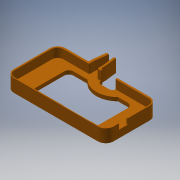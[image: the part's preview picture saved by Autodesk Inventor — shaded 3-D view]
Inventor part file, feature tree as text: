
AUTODESK INVENTOR PART (.ipt)
format: ipt  version: 2017 (Build 210142000, 142)  size: 312,832 bytes
history: native  units: in
note: dims shown in document units (in); Inventor stores cm internally (conversion verified against a paired STEP export)
features: extrude x11, sketch x11, fillet x7, thicken_offset x1
ambient origin geometry x8: Origin, YZ Plane, XZ Plane, XY Plane, X Axis, Y Axis, Z Axis, Center Point
bodies: Solid1 (feature_tree)
feature tree (30):
  extrude  "Extrusion1"  Depth=2.655in
  extrude  "Extrusion2"  Depth=0.5in TaperAngle=0.0deg
  fillet  "Fillet1"  Radius=0.2in
  fillet  "Fillet2"  Radius=0.3in
  extrude  "Extrusion3"  Depth=0.42in
  extrude  "Extrusion4"  Depth=0.125in
  extrude  "Extrusion5"  Depth=0.125in
  fillet  "Fillet3"  Radius=0.125in
  fillet  "Fillet4"  Radius=0.125in
  fillet  "Fillet5"  Radius=0.125in
  extrude  "Extrusion6"  Depth=0.125in TaperAngle=0.0deg
  fillet  "Fillet6"  Radius=0.06in
  extrude  "Extrusion8"  Depth=0.04in
  fillet  "Fillet7"  Radius=0.25in
  extrude  "Extrusion10"  TaperAngle=0.0deg  [1 undecoded]
  extrude  "Extrusion11"  Depth=0.16in TaperAngle=0.0deg
  extrude  "Extrusion13"  Depth=1.1887in
  thicken_offset  "Thicken1"
  extrude  "Extrusion12"  Depth=0.5in
  sketch  "Sketch1"  dims[d0=5.265in d1=2.655in]
  sketch  "Sketch2"  dims[d2=0.08in d3=0.5in d4=0.0in d5=0.2in d6=0.0in d7=0.3in]
  sketch  "Sketch3"  dims[d8=0.425in d9=0.42in]
  sketch  "Sketch4"  dims[d10=0.125in d11=0.0in d14=0.2275in]
  sketch  "Sketch5"  dims[d15=0.9in d17=0.125in d18=0.125in d19=0.125in d20=0.125in]
  sketch  "Sketch6"  dims[d21=0.0in d22=0.0in d23=0.125in d24=0.0in d25=0.06in]
  sketch  "Sketch8"  dims[d26=0.06in d27=0.04in d29=0.25in]
  sketch  "Sketch10"  dims[d30=2.75in d31=0.0in d32=0.0in]
  sketch  "Sketch11"  dims[d33=0.16in d43=1.0in d44=0.0in]
  sketch  "Sketch12"  dims[d45=1.1887in d46=1.1887in]
  sketch  "Sketch13"  dims[d47=0.2549in d50=1.932in d53=0.9in d54=0.9in d55=0.3in d56=0.3in d57=0.25in d58=1.0in d59=0.0in d61=0.8in d62=0.48in d63=0.88in d64=0.3in d65=0.0in d66=2.0in d67=0.0in d72=0.0in d73=0.0in d74=0.875in d75=1.0in d77=0.04in d78=1.0in d79=0.0in d80=0.5in d81=0.5in]
note: 1 required parameter value undecoded (feature->parameter linkage not recoverable at this tier; creation-order binding heuristic only, values carry confidence <= 0.55)
